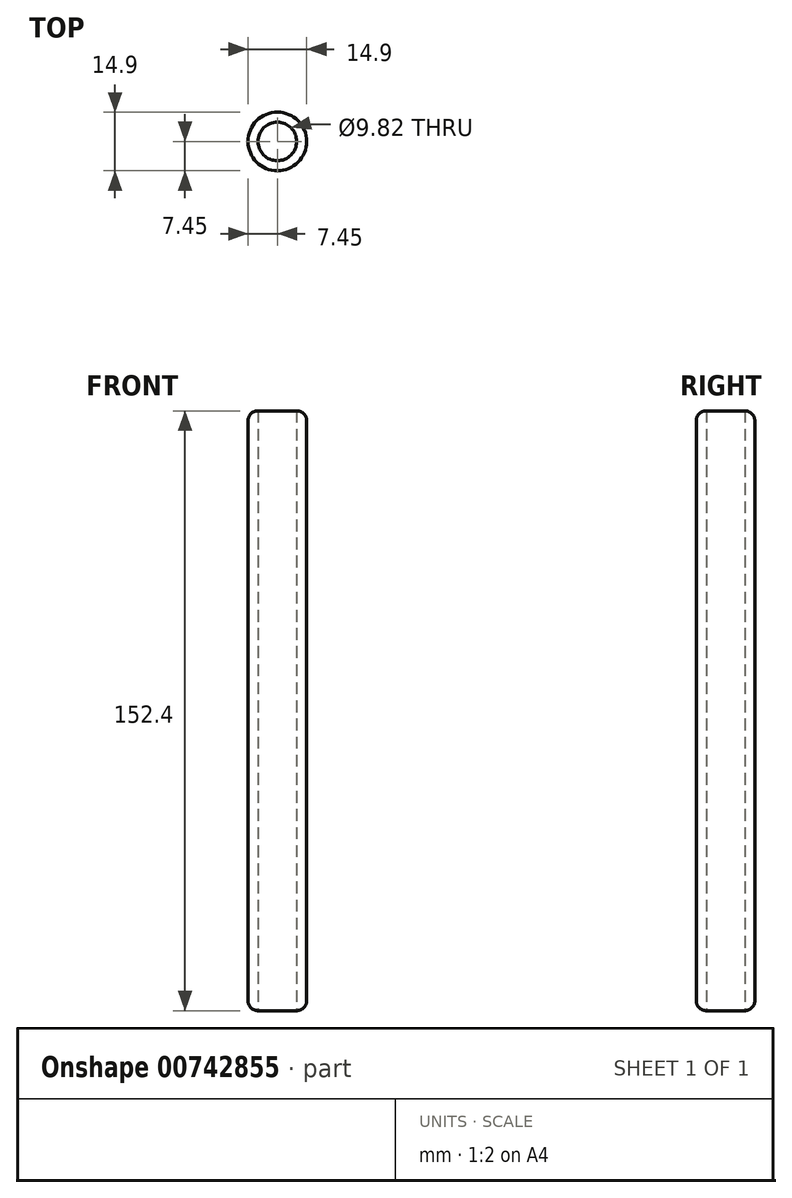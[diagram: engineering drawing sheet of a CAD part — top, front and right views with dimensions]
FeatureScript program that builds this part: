
annotation { "Feature Type Name" : "Feature", "Feature Type Description" : "" }
export const myFeature = defineFeature(function(context is Context, id is Id, definition is map)
    precondition{}
    {
        {
            var Q0;
            Q0=qCreatedBy(makeId("Front.planeOp"),FACE);
            var sketch = newSketch(context, id + "F0", { "sketchPlane" : qUnion([Q0])});
            skLineSegment(sketch, "E0.bottom", {"start": v(-4.9, -75.3) * mm, "end": v(-7.45, -75.3) * mm});
            skLineSegment(sketch, "E0.top", {"start": v(-4.9, 77.1) * mm, "end": v(-7.45, 77.1) * mm});
            skLineSegment(sketch, "E0.left", {"start": v(-4.9, -75.3) * mm, "end": v(-4.9, 77.1) * mm});
            skLineSegment(sketch, "E0.right", {"start": v(-7.45, -75.3) * mm, "end": v(-7.45, 77.1) * mm});
            skLineSegment(sketch, "E1", {"start": v(0, -76) * mm, "end": v(0, 73.8) * mm});
            skSolve(sketch);
        }
        {
            var Q0;
            Q0 = qSketchRegion(id + "F0", true);
            var Q1;
            Q1=sQuery(id+"F0.wireOp",EDGE,"E1");
            revolve(context, id + "F1", {"surfaceOperationType" : NewSurfaceOperationType.NEW, "entities" : qUnion([Q0]), "axis" : qUnion([Q1]), "revolveType" : RevolveType.FULL});
        }
        {
            var Q0;
            Q0=makeQuery(id+"F1.opRevolve","SWEPT_EDGE",EDGE,{"disambiguationData":[OSD([sQuery(id+"F0.wireOp",EDGE,"E0.top"),sQuery(id+"F0.wireOp",EDGE,"E0.right")])]});
            var Q1;
            Q1=makeQuery(id+"F1.opRevolve","SWEPT_EDGE",EDGE,{"disambiguationData":[OSD([sQuery(id+"F0.wireOp",EDGE,"E0.bottom"),sQuery(id+"F0.wireOp",EDGE,"E0.right")])]});
            fillet(context, id + "F2", {"entities" : qUnion([Q0, Q1]), "radius" : 2.54 * mm, "tangentPropagation" : true, "allowEdgeOverflow" : false});
        }
    });
